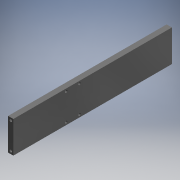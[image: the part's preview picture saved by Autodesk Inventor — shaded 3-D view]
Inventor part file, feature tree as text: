
AUTODESK INVENTOR PART (.ipt)
format: ipt  version: 2019 (Build 230136000, 136)  size: 122,880 bytes
history: native  units: mm (DEFAULTED — no unit token found)
features: extrude x3, sketch x3, plane x2, mirror x2
ambient origin geometry x8: Origin, YZ Plane, XZ Plane, XY Plane, X Axis, Y Axis, Z Axis, Center Point
bodies: Solid1 (feature_tree)
feature tree (10):
  extrude  "Extrusion1"  Depth=38.1mm
  extrude  "Extrusion2"  Depth=190.5mm
  plane  "Work Plane1"
  mirror  "Mirror1"
  extrude  "Extrusion3"  Depth=6.35mm
  plane  "Work Plane2"
  mirror  "Mirror2"
  sketch  "Sketch1"  dims[d0=6.35mm d1=38.1mm]
  sketch  "Sketch2"  dims[d2=190.5mm d3=0.0mm d4=3.048mm]
  sketch  "Sketch3"  dims[d5=3.048mm d6=3.175mm d7=3.175mm d8=3.175mm d9=3.175mm d10=6.35mm d11=0.0mm d12=3.048mm d13=3.048mm d14=16.002mm d15=63.5mm d16=110.998mm d17=2.921mm d18=2.921mm d19=6.35mm d20=0.0mm]
